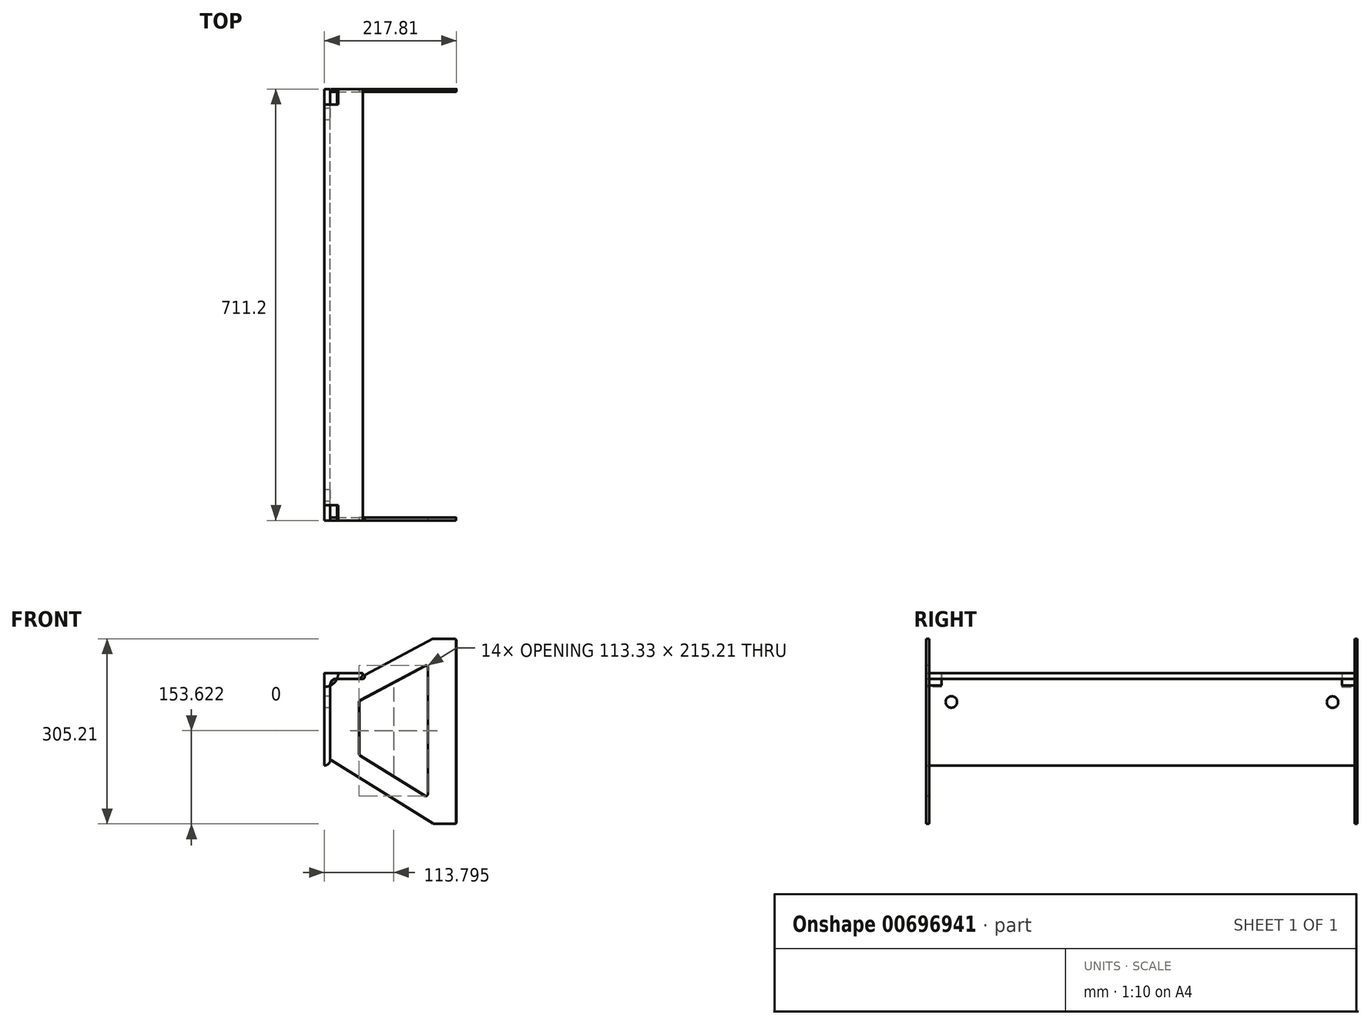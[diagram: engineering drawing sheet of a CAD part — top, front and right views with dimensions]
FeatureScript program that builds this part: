
annotation { "Feature Type Name" : "Feature", "Feature Type Description" : "" }
export const myFeature = defineFeature(function(context is Context, id is Id, definition is map)
    precondition{}
    {
        {
            var Q0;
            Q0=qCreatedBy(makeId("Front.planeOp"),FACE);
            var sketch = newSketch(context, id + "F0", { "sketchPlane" : qUnion([Q0])});
            skLineSegment(sketch, "E0", {"start": v(-47.1, 105) * mm, "end": v(-47.1, -47.15) * mm});
            skLineSegment(sketch, "E1", {"start": v(-47.1, -47.15) * mm, "end": v(-47.1, -47.15) * mm});
            skLineSegment(sketch, "E2", {"start": v(-37.57, -37.63) * mm, "end": v(-37.57, 86.2) * mm});
            skLineSegment(sketch, "E3", {"start": v(-28.05, 95.72) * mm, "end": v(6.88, 95.72) * mm});
            skLineSegment(sketch, "E4", {"start": v(-46.84, 105.25) * mm, "end": v(16.4, 105.25) * mm});
            skLineSegment(sketch, "E5", {"start": v(16.4, 105.25) * mm, "end": v(16.4, 105.25) * mm});
            skPoint(sketch, "E6.visualSharp", {"position": v(-37.57, 95.72) * mm});
            skArc(sketch, "E6.filletArc", {"start": v(-28.05, 95.72) * mm, "mid": v(-34.78, 92.93) * mm, "end": v(-37.57, 86.2) * mm});
            skPoint(sketch, "E7.visualSharp", {"position": v(-37.57, -47.15) * mm});
            skArc(sketch, "E7.filletArc", {"start": v(-47.1, -47.15) * mm, "mid": v(-40.36, -44.36) * mm, "end": v(-37.57, -37.63) * mm});
            skPoint(sketch, "E8.visualSharp", {"position": v(16.4, 95.72) * mm});
            skArc(sketch, "E8.filletArc", {"start": v(6.88, 95.72) * mm, "mid": v(13.61, 98.51) * mm, "end": v(16.4, 105.25) * mm});
            skPoint(sketch, "E9.visualSharp", {"position": v(-47.1, 105.25) * mm});
            skArc(sketch, "E9.filletArc", {"start": v(-46.84, 105.25) * mm, "mid": v(-47.02, 105.17) * mm, "end": v(-47.1, 105) * mm});
            skSolve(sketch);
        }
        {
            var Q0;
            Q0=makeQuery(id+"F0.imprint","IMPRINT",FACE,{"disambiguationData":[TD([[makeQuery(id+"F0.imprint","IMPRINT",EDGE,{"derivedFrom":sQuery(id+"F0.wireOp",EDGE,"E0")}),1.0]])]});
            extrude(context, id + "F1", {"entities" : qUnion([Q0]), "depth" : 711.2 * mm, "offsetDistance" : 25.4 * mm});
        }
        {
            var Q0;
            Q0=makeQuery(id+"F1.opExtrude","CAP_FACE",FACE,{"disambiguationData":[OSD([sQuery(id+"F0.wireOp",EDGE,"E0"),sQuery(id+"F0.wireOp",EDGE,"E2"),sQuery(id+"F0.wireOp",EDGE,"E3"),sQuery(id+"F0.wireOp",EDGE,"E4"),sQuery(id+"F0.wireOp",EDGE,"E6.filletArc"),sQuery(id+"F0.wireOp",EDGE,"E7.filletArc"),sQuery(id+"F0.wireOp",EDGE,"E8.filletArc"),sQuery(id+"F0.wireOp",EDGE,"E9.filletArc")])],"isStart":false});
            var sketch = newSketch(context, id + "F2", { "sketchPlane" : qUnion([Q0])});
            skCircle(sketch, "E10", {"center": v(-46.67, 104.81) * mm, "radius": 22.23 * mm});
            skSolve(sketch);
        }
        {
            var Q0;
            Q0 = qSketchRegion(id + "F2", true);
            extrude(context, id + "F3", {"entities" : qUnion([Q0]), "operationType" : NewBodyOperationType.REMOVE, "oppositeDirection" : true, "depth" : 25.4 * mm, "offsetDistance" : 25.4 * mm});
        }
        {
            var Q0;
            Q0=makeQuery(id+"F1.opExtrude","CAP_FACE",FACE,{"disambiguationData":[OSD([sQuery(id+"F0.wireOp",EDGE,"E0"),sQuery(id+"F0.wireOp",EDGE,"E2"),sQuery(id+"F0.wireOp",EDGE,"E3"),sQuery(id+"F0.wireOp",EDGE,"E4"),sQuery(id+"F0.wireOp",EDGE,"E6.filletArc"),sQuery(id+"F0.wireOp",EDGE,"E7.filletArc"),sQuery(id+"F0.wireOp",EDGE,"E8.filletArc"),sQuery(id+"F0.wireOp",EDGE,"E9.filletArc")])],"isStart":true});
            var sketch = newSketch(context, id + "F4", { "sketchPlane" : qUnion([Q0])});
            skCircle(sketch, "E11", {"center": v(46.67, 104.81) * mm, "radius": 22.23 * mm});
            skSolve(sketch);
        }
        {
            var Q0;
            Q0 = qSketchRegion(id + "F4", true);
            extrude(context, id + "F5", {"entities" : qUnion([Q0]), "operationType" : NewBodyOperationType.REMOVE, "oppositeDirection" : true, "depth" : 25.4 * mm, "offsetDistance" : 25.4 * mm});
        }
        {
            var Q0;
            Q0=makeQuery(id+"F1.opExtrude","SWEPT_FACE",FACE,{"disambiguationData":[OSD([sQuery(id+"F0.wireOp",EDGE,"E0")])]});
            var sketch = newSketch(context, id + "F6", { "sketchPlane" : qUnion([Q0])});
            skCircle(sketch, "E12", {"center": v(41.27, 57.37) * mm, "radius": 9.53 * mm});
            skCircle(sketch, "E13", {"center": v(669.93, 57.62) * mm, "radius": 9.53 * mm});
            skSolve(sketch);
        }
        {
            var Q0;
            Q0 = qSketchRegion(id + "F6", true);
            extrude(context, id + "F7", {"entities" : qUnion([Q0]), "operationType" : NewBodyOperationType.REMOVE, "endBound" : BoundingType.THROUGH_ALL, "oppositeDirection" : true, "depth" : 25.4 * mm, "offsetDistance" : 25.4 * mm});
        }
        {
            var Q0;
            {var subQ0=sQuery(id+"F0.wireOp",EDGE,"E0");var subQ1=sQuery(id+"F0.wireOp",EDGE,"E2");var subQ2=sQuery(id+"F0.wireOp",EDGE,"E7.filletArc");Q0=makeQuery(id+"F3.boolean.opBoolean","SPLIT",FACE,{"disambiguationData":[TD([makeQuery(id+"F1.opExtrude","SWEPT_FACE",FACE,{"disambiguationData":[OSD([subQ0])]})])],"derivedFrom":makeQuery(id+"F1.opExtrude","CAP_FACE",FACE,{"disambiguationData":[OSD([subQ0,subQ1,sQuery(id+"F0.wireOp",EDGE,"E3"),sQuery(id+"F0.wireOp",EDGE,"E4"),sQuery(id+"F0.wireOp",EDGE,"E6.filletArc"),subQ2,sQuery(id+"F0.wireOp",EDGE,"E8.filletArc"),sQuery(id+"F0.wireOp",EDGE,"E9.filletArc")])],"isStart":false})});}
            var sketch = newSketch(context, id + "F8", { "sketchPlane" : qUnion([Q0])});
            skLineSegment(sketch, "E14", {"start": v(20.8, 102.68) * mm, "end": v(131.17, 161.45) * mm});
            skLineSegment(sketch, "E15", {"start": v(132.66, 161.82) * mm, "end": v(166.79, 161.82) * mm});
            skLineSegment(sketch, "E16", {"start": v(169.96, 158.65) * mm, "end": v(169.96, -139.8) * mm});
            skLineSegment(sketch, "E17", {"start": v(166.79, -142.98) * mm, "end": v(133.47, -142.98) * mm});
            skLineSegment(sketch, "E18", {"start": v(131.8, -142.5) * mm, "end": v(-36.07, -38.56) * mm});
            skLineSegment(sketch, "E19", {"start": v(-37.57, -35.86) * mm, "end": v(-37.57, 84.53) * mm});
            skArc(sketch, "E20", {"start": v(-26.54, 95.76) * mm, "mid": v(-34.35, 92.4) * mm, "end": v(-37.57, 84.53) * mm});
            skLineSegment(sketch, "E21", {"start": v(123.36, 114.66) * mm, "end": v(123.36, -94.2) * mm});
            skLineSegment(sketch, "E22", {"start": v(118.51, -96.9) * mm, "end": v(11.53, -30.66) * mm});
            skLineSegment(sketch, "E23", {"start": v(10.03, -27.96) * mm, "end": v(10.03, 57.69) * mm});
            skLineSegment(sketch, "E24", {"start": v(11.71, 60.5) * mm, "end": v(118.7, 117.47) * mm});
            skPoint(sketch, "E25.visualSharp", {"position": v(131.86, 161.82) * mm});
            skArc(sketch, "E25.filletArc", {"start": v(132.66, 161.82) * mm, "mid": v(131.89, 161.73) * mm, "end": v(131.17, 161.45) * mm});
            skPoint(sketch, "E26.visualSharp", {"position": v(169.96, 161.82) * mm});
            skArc(sketch, "E26.filletArc", {"start": v(169.96, 158.65) * mm, "mid": v(169.04, 160.9) * mm, "end": v(166.79, 161.82) * mm});
            skPoint(sketch, "E27.visualSharp", {"position": v(123.36, 119.95) * mm});
            skArc(sketch, "E27.filletArc", {"start": v(123.36, 114.66) * mm, "mid": v(121.82, 117.39) * mm, "end": v(118.7, 117.47) * mm});
            skPoint(sketch, "E28.visualSharp", {"position": v(10.03, 59.6) * mm});
            skArc(sketch, "E28.filletArc", {"start": v(11.71, 60.5) * mm, "mid": v(10.48, 59.32) * mm, "end": v(10.03, 57.69) * mm});
            skPoint(sketch, "E29.visualSharp", {"position": v(10.03, -29.73) * mm});
            skArc(sketch, "E29.filletArc", {"start": v(10.03, -27.96) * mm, "mid": v(10.43, -29.5) * mm, "end": v(11.53, -30.66) * mm});
            skPoint(sketch, "E30.visualSharp", {"position": v(123.36, -99.9) * mm});
            skArc(sketch, "E30.filletArc", {"start": v(118.51, -96.9) * mm, "mid": v(121.73, -96.97) * mm, "end": v(123.36, -94.2) * mm});
            skPoint(sketch, "E31.visualSharp", {"position": v(169.96, -142.98) * mm});
            skArc(sketch, "E31.filletArc", {"start": v(166.79, -142.98) * mm, "mid": v(169.04, -142.05) * mm, "end": v(169.96, -139.8) * mm});
            skPoint(sketch, "E32.visualSharp", {"position": v(132.56, -142.98) * mm});
            skArc(sketch, "E32.filletArc", {"start": v(131.8, -142.5) * mm, "mid": v(132.6, -142.86) * mm, "end": v(133.47, -142.98) * mm});
            skPoint(sketch, "E33.visualSharp", {"position": v(-37.57, -37.63) * mm});
            skArc(sketch, "E33.filletArc", {"start": v(-37.57, -35.86) * mm, "mid": v(-37.17, -37.4) * mm, "end": v(-36.07, -38.56) * mm});
            skPoint(sketch, "E34.visualSharp", {"position": v(11.42, 101.78) * mm});
            skArc(sketch, "E34.filletArc", {"start": v(11.67, 101.78) * mm, "mid": v(11.42, 101.77) * mm, "end": v(11.17, 101.74) * mm});
            skLineSegment(sketch, "E35", {"start": v(-26.54, 95.76) * mm, "end": v(15.95, 95.76) * mm});
            skLineSegment(sketch, "E36", {"start": v(19.12, 99.87) * mm, "end": v(19.12, 98.93) * mm});
            skPoint(sketch, "E37.visualSharp", {"position": v(19.12, 101.78) * mm});
            skArc(sketch, "E37.filletArc", {"start": v(20.8, 102.68) * mm, "mid": v(19.58, 101.5) * mm, "end": v(19.12, 99.87) * mm});
            skPoint(sketch, "E38.visualSharp", {"position": v(19.12, 95.76) * mm});
            skArc(sketch, "E38.filletArc", {"start": v(15.95, 95.76) * mm, "mid": v(18.2, 96.69) * mm, "end": v(19.12, 98.93) * mm});
            skSolve(sketch);
        }
        {
            var Q0;
            Q0=makeQuery(id+"F8.imprint","IMPRINT",FACE,{"disambiguationData":[TD([[makeQuery(id+"F8.imprint","IMPRINT",EDGE,{"derivedFrom":sQuery(id+"F8.wireOp",EDGE,"E14")}),-1.0]])]});
            extrude(context, id + "F9", {"entities" : qUnion([Q0]), "oppositeDirection" : true, "depth" : 4.57 * mm, "offsetDistance" : 25.4 * mm});
        }
        {
            var Q0;
            Q0=qCreatedBy(makeId("Front.planeOp"),FACE);
            var sketch = newSketch(context, id + "F10", { "sketchPlane" : qUnion([Q0])});
            skLineSegment(sketch, "E39", {"start": v(21.55, 102.26) * mm, "end": v(131.9, 161.04) * mm});
            skLineSegment(sketch, "E40", {"start": v(133.4, 161.4) * mm, "end": v(167.53, 161.4) * mm});
            skLineSegment(sketch, "E41", {"start": v(170.7, 158.23) * mm, "end": v(170.7, -140.22) * mm});
            skLineSegment(sketch, "E42", {"start": v(167.53, -143.4) * mm, "end": v(134.21, -143.4) * mm});
            skLineSegment(sketch, "E43", {"start": v(132.54, -142.92) * mm, "end": v(-35.33, -38.97) * mm});
            skLineSegment(sketch, "E44", {"start": v(-36.83, -36.27) * mm, "end": v(-36.83, 84.12) * mm});
            skArc(sketch, "E45", {"start": v(-25.8, 95.34) * mm, "mid": v(-33.61, 91.99) * mm, "end": v(-36.83, 84.12) * mm});
            skLineSegment(sketch, "E46", {"start": v(124.1, 114.25) * mm, "end": v(124.1, -94.61) * mm});
            skLineSegment(sketch, "E47", {"start": v(119.26, -97.31) * mm, "end": v(12.28, -31.07) * mm});
            skLineSegment(sketch, "E48", {"start": v(10.77, -28.37) * mm, "end": v(10.77, 57.27) * mm});
            skLineSegment(sketch, "E49", {"start": v(12.46, 60.08) * mm, "end": v(119.44, 117.05) * mm});
            skPoint(sketch, "E50.visualSharp", {"position": v(132.6, 161.4) * mm});
            skArc(sketch, "E50.filletArc", {"start": v(133.4, 161.4) * mm, "mid": v(132.63, 161.31) * mm, "end": v(131.9, 161.04) * mm});
            skPoint(sketch, "E51.visualSharp", {"position": v(170.7, 161.4) * mm});
            skArc(sketch, "E51.filletArc", {"start": v(170.7, 158.23) * mm, "mid": v(169.78, 160.48) * mm, "end": v(167.53, 161.4) * mm});
            skPoint(sketch, "E52.visualSharp", {"position": v(124.1, 119.54) * mm});
            skArc(sketch, "E52.filletArc", {"start": v(124.1, 114.25) * mm, "mid": v(122.56, 116.97) * mm, "end": v(119.44, 117.05) * mm});
            skPoint(sketch, "E53.visualSharp", {"position": v(10.77, 59.18) * mm});
            skArc(sketch, "E53.filletArc", {"start": v(12.46, 60.08) * mm, "mid": v(11.23, 58.9) * mm, "end": v(10.77, 57.27) * mm});
            skPoint(sketch, "E54.visualSharp", {"position": v(10.77, -30.14) * mm});
            skArc(sketch, "E54.filletArc", {"start": v(10.77, -28.37) * mm, "mid": v(11.17, -29.92) * mm, "end": v(12.28, -31.07) * mm});
            skPoint(sketch, "E55.visualSharp", {"position": v(124.1, -100.32) * mm});
            skArc(sketch, "E55.filletArc", {"start": v(119.26, -97.31) * mm, "mid": v(122.47, -97.39) * mm, "end": v(124.1, -94.61) * mm});
            skPoint(sketch, "E56.visualSharp", {"position": v(170.7, -143.4) * mm});
            skArc(sketch, "E56.filletArc", {"start": v(167.53, -143.4) * mm, "mid": v(169.78, -142.46) * mm, "end": v(170.7, -140.22) * mm});
            skPoint(sketch, "E57.visualSharp", {"position": v(133.3, -143.4) * mm});
            skArc(sketch, "E57.filletArc", {"start": v(132.54, -142.92) * mm, "mid": v(133.34, -143.27) * mm, "end": v(134.21, -143.4) * mm});
            skPoint(sketch, "E58.visualSharp", {"position": v(-36.83, -38.04) * mm});
            skArc(sketch, "E58.filletArc", {"start": v(-36.83, -36.27) * mm, "mid": v(-36.43, -37.82) * mm, "end": v(-35.33, -38.97) * mm});
            skPoint(sketch, "E59.visualSharp", {"position": v(12.16, 101.36) * mm});
            skArc(sketch, "E59.filletArc", {"start": v(12.41, 101.36) * mm, "mid": v(12.16, 101.36) * mm, "end": v(11.91, 101.33) * mm});
            skLineSegment(sketch, "E60", {"start": v(-25.8, 95.34) * mm, "end": v(16.7, 95.34) * mm});
            skLineSegment(sketch, "E61", {"start": v(19.87, 99.46) * mm, "end": v(19.87, 98.52) * mm});
            skPoint(sketch, "E62.visualSharp", {"position": v(19.87, 101.36) * mm});
            skArc(sketch, "E62.filletArc", {"start": v(21.55, 102.26) * mm, "mid": v(20.32, 101.1) * mm, "end": v(19.87, 99.46) * mm});
            skPoint(sketch, "E63.visualSharp", {"position": v(19.87, 95.34) * mm});
            skArc(sketch, "E63.filletArc", {"start": v(16.7, 95.34) * mm, "mid": v(18.94, 96.27) * mm, "end": v(19.87, 98.52) * mm});
            skSolve(sketch);
        }
        {
            var Q0;
            Q0=makeQuery(id+"F10.imprint","IMPRINT",FACE,{"disambiguationData":[TD([[makeQuery(id+"F10.imprint","IMPRINT",EDGE,{"derivedFrom":sQuery(id+"F10.wireOp",EDGE,"E39")}),-1.0]])]});
            extrude(context, id + "F11", {"entities" : qUnion([Q0]), "depth" : 4.57 * mm, "offsetDistance" : 25.4 * mm});
        }
    });
